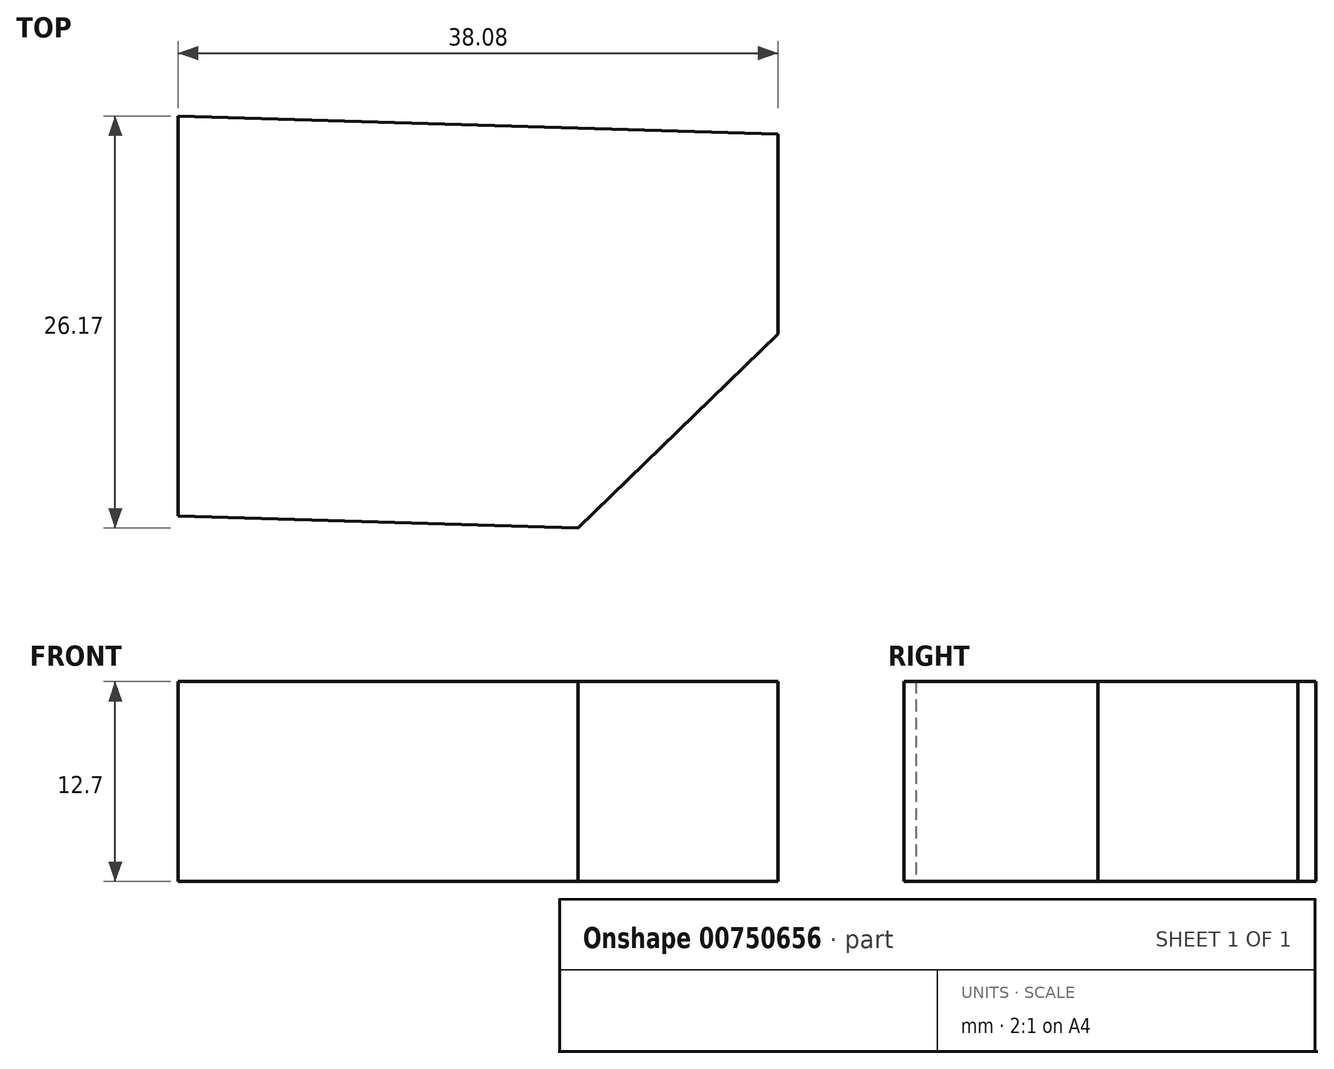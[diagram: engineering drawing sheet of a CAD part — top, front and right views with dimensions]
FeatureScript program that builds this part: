
annotation { "Feature Type Name" : "Feature", "Feature Type Description" : "" }
export const myFeature = defineFeature(function(context is Context, id is Id, definition is map)
    precondition{}
    {
        {
            var Q0;
            Q0=qCreatedBy(makeId("Top.planeOp"),FACE);
            var sketch = newSketch(context, id + "F0", { "sketchPlane" : qUnion([Q0])});
            skLineSegment(sketch, "E0", {"start": v(-38.08, 26.56) * mm, "end": v(-38.08, 1.16) * mm});
            skLineSegment(sketch, "E1", {"start": v(-38.08, 1.16) * mm, "end": v(0, 0) * mm});
            skLineSegment(sketch, "E2", {"start": v(0, 0) * mm, "end": v(0, 25.4) * mm});
            skLineSegment(sketch, "E3", {"start": v(0, 25.4) * mm, "end": v(-38.08, 26.56) * mm});
            skSolve(sketch);
        }
        {
            var Q0;
            Q0=makeQuery(id+"F0.imprint","IMPRINT",FACE,{"disambiguationData":[TD([[makeQuery(id+"F0.imprint","IMPRINT",EDGE,{"derivedFrom":sQuery(id+"F0.wireOp",EDGE,"E0")}),1.0]])]});
            extrude(context, id + "F1", {"entities" : qUnion([Q0]), "depth" : 12.7 * mm, "offsetDistance" : 25.4 * mm});
        }
        {
            var Q0;
            Q0=makeQuery(id+"F1.opExtrude","CAP_FACE",FACE,{"disambiguationData":[OSD([sQuery(id+"F0.wireOp",EDGE,"E0"),sQuery(id+"F0.wireOp",EDGE,"E1"),sQuery(id+"F0.wireOp",EDGE,"E2"),sQuery(id+"F0.wireOp",EDGE,"E3")])],"isStart":false});
            var sketch = newSketch(context, id + "F2", { "sketchPlane" : qUnion([Q0])});
            skLineSegment(sketch, "E4", {"start": v(0, 12.7) * mm, "end": v(-12.68, 0.39) * mm});
            skSolve(sketch);
        }
        {
            var Q0;
            Q0 = qSketchRegion(id + "F2", true);
            var Q1;
            {var subQ0=sQuery(id+"F2.wireOp",EDGE,"E4");Q1=makeQuery(id+"F2.imprint","IMPRINT",FACE,{"disambiguationData":[TD([[makeQuery(id+"F2.imprint","IMPRINT",EDGE,{"derivedFrom":subQ0}),1.0]])]});}
            var Q2;
            {var subQ2=sQuery(id+"F2.wireOp",EDGE,"E4");Q2=makeQuery(id+"F2.imprint","IMPRINT",FACE,{"disambiguationData":[TD([[makeQuery(id+"F2.imprint","IMPRINT",EDGE,{"derivedFrom":subQ2}),-1.0]])]});}
            extrude(context, id + "F3", {"entities" : qUnion([Q0, Q1, Q2]), "operationType" : NewBodyOperationType.REMOVE, "oppositeDirection" : true, "depth" : 25.4 * mm, "offsetDistance" : 25.4 * mm});
        }
        {
            var Q0;
            Q0 = qSketchRegion(id + "F0", true);
            extrude(context, id + "F4", {"entities" : qUnion([Q0]), "depth" : 12.7 * mm, "offsetDistance" : 25.4 * mm});
        }
        {
            var Q0;
            Q0=makeQuery(id+"F4.opExtrude","CAP_FACE",FACE,{"disambiguationData":[OSD([sQuery(id+"F0.wireOp",EDGE,"E0"),sQuery(id+"F0.wireOp",EDGE,"E1"),sQuery(id+"F0.wireOp",EDGE,"E2"),sQuery(id+"F0.wireOp",EDGE,"E3")])],"isStart":false});
            var sketch = newSketch(context, id + "F5", { "sketchPlane" : qUnion([Q0])});
            skLineSegment(sketch, "E5", {"start": v(0, 12.7) * mm, "end": v(-12.7, 0.39) * mm});
            skSolve(sketch);
        }
        {
            var Q0;
            {var subQ0=sQuery(id+"F5.wireOp",EDGE,"E5");Q0=makeQuery(id+"F5.imprint","IMPRINT",FACE,{"disambiguationData":[TD([[makeQuery(id+"F5.imprint","IMPRINT",EDGE,{"derivedFrom":subQ0}),1.0]])]});}
            extrude(context, id + "F6", {"entities" : qUnion([Q0]), "operationType" : NewBodyOperationType.REMOVE, "endBound" : BoundingType.THROUGH_ALL, "oppositeDirection" : true, "depth" : 25.4 * mm, "offsetDistance" : 25.4 * mm});
        }
    });
